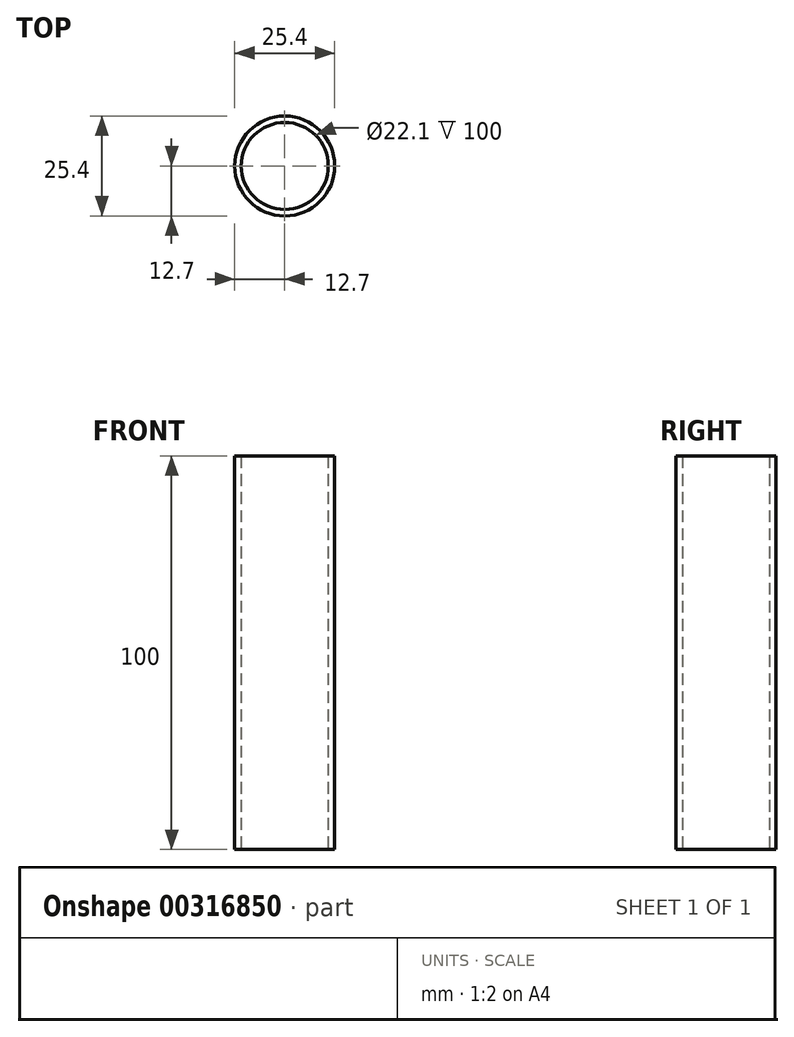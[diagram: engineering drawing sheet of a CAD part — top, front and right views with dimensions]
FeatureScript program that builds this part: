
annotation { "Feature Type Name" : "Feature", "Feature Type Description" : "" }
export const myFeature = defineFeature(function(context is Context, id is Id, definition is map)
    precondition{}
    {
        {
            var Q0;
            Q0=qCreatedBy(makeId("Front.planeOp"),FACE);
            var sketch = newSketch(context, id + "F0", { "sketchPlane" : qUnion([Q0])});
            skLineSegment(sketch, "E0", {"start": v(0, 0) * mm, "end": v(0, 20.44) * mm, "construction": true});
            skLineSegment(sketch, "E1.bottom", {"start": v(-12.7, 100) * mm, "end": v(-11.05, 100) * mm});
            skLineSegment(sketch, "E1.top", {"start": v(-12.7, 0) * mm, "end": v(-11.05, 0) * mm});
            skLineSegment(sketch, "E1.left", {"start": v(-12.7, 100) * mm, "end": v(-12.7, 0) * mm});
            skLineSegment(sketch, "E1.right", {"start": v(-11.05, 100) * mm, "end": v(-11.05, 0) * mm});
            skSolve(sketch);
        }
        {
            var Q0;
            Q0 = qSketchRegion(id + "F0", true);
            var Q1;
            Q1=sQuery(id+"F0.wireOp",EDGE,"E0");
            revolve(context, id + "F1", {"entities" : qUnion([Q0]), "axis" : qUnion([Q1]), "revolveType" : RevolveType.FULL});
        }
    });
